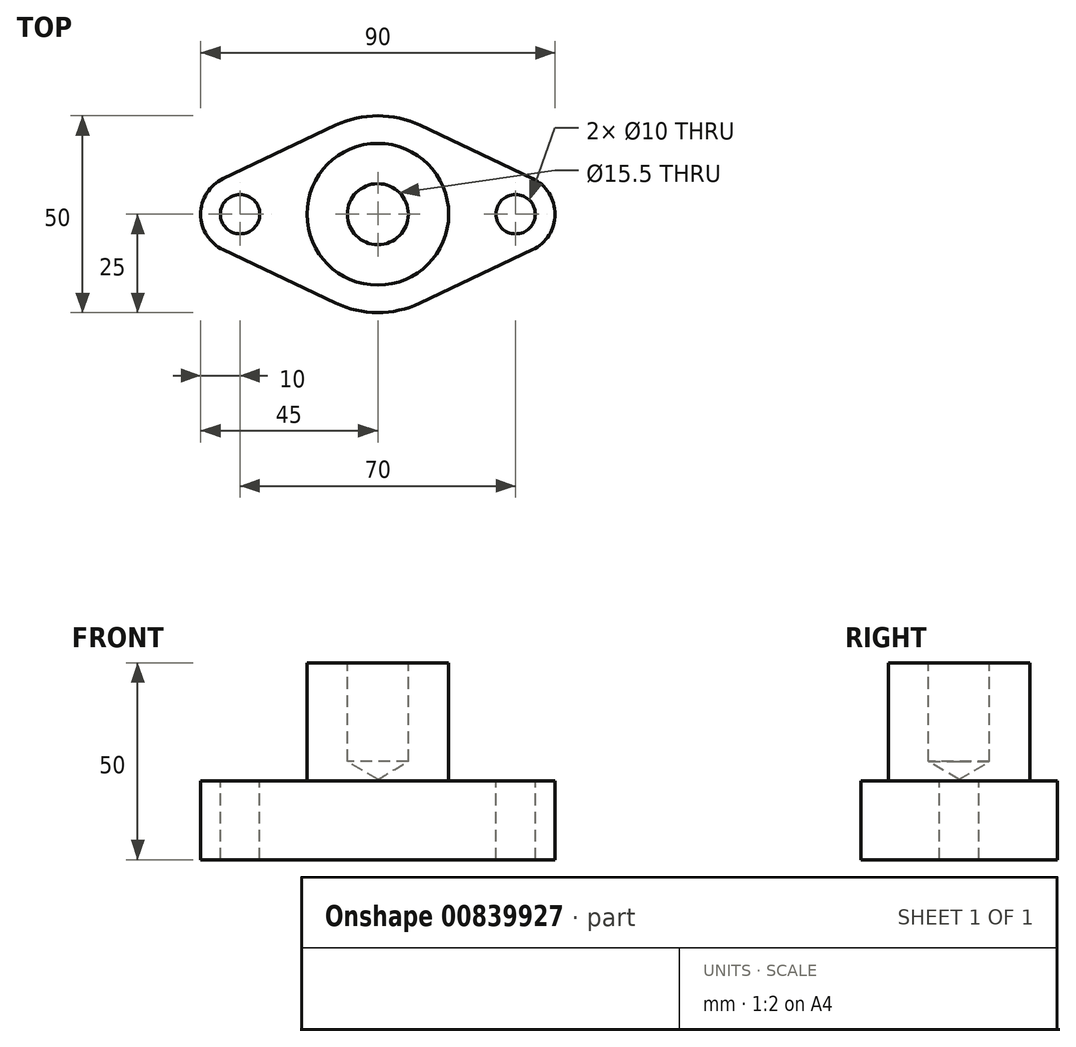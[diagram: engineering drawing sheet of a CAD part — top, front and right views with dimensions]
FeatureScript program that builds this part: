
annotation { "Feature Type Name" : "Feature", "Feature Type Description" : "" }
export const myFeature = defineFeature(function(context is Context, id is Id, definition is map)
    precondition{}
    {
        {
            var Q0;
            Q0=qCreatedBy(makeId("Top.planeOp"),FACE);
            var sketch = newSketch(context, id + "F0", { "sketchPlane" : qUnion([Q0])});
            skLineSegment(sketch, "E0", {"start": v(-39.29, 9.04) * mm, "end": v(-10.71, 22.59) * mm});
            skLineSegment(sketch, "E1", {"start": v(10.71, 22.59) * mm, "end": v(39.29, 9.04) * mm});
            skLineSegment(sketch, "E2", {"start": v(-39.29, -9.04) * mm, "end": v(-10.71, -22.59) * mm});
            skLineSegment(sketch, "E3", {"start": v(10.65, -22.62) * mm, "end": v(39.29, -9.04) * mm});
            skArc(sketch, "E4", {"start": v(-10.71, 22.59) * mm, "mid": v(0, 25) * mm, "end": v(10.71, 22.59) * mm});
            skArc(sketch, "E5", {"start": v(10.65, -22.62) * mm, "mid": v(-0.07, -25) * mm, "end": v(-10.77, -22.56) * mm});
            skArc(sketch, "E6", {"start": v(-39.29, 9.04) * mm, "mid": v(-45, 0) * mm, "end": v(-39.29, -9.04) * mm});
            skArc(sketch, "E7", {"start": v(39.29, 9.04) * mm, "mid": v(45, 0) * mm, "end": v(39.29, -9.04) * mm});
            skSolve(sketch);
        }
        {
            var Q0;
            Q0=makeQuery(id+"F0.imprint","IMPRINT",FACE,{"disambiguationData":[TD([[makeQuery(id+"F0.imprint","IMPRINT",EDGE,{"derivedFrom":sQuery(id+"F0.wireOp",EDGE,"E0")}),-1.0]])]});
            extrude(context, id + "F1", {"entities" : qUnion([Q0]), "depth" : 20 * mm, "offsetDistance" : 25 * mm});
        }
        {
            var Q0;
            Q0=makeQuery(id+"F1.opExtrude","CAP_FACE",FACE,{"disambiguationData":[OSD([sQuery(id+"F0.wireOp",EDGE,"E0"),sQuery(id+"F0.wireOp",EDGE,"E1"),sQuery(id+"F0.wireOp",EDGE,"E2"),sQuery(id+"F0.wireOp",EDGE,"E3"),sQuery(id+"F0.wireOp",EDGE,"E4"),sQuery(id+"F0.wireOp",EDGE,"E5"),sQuery(id+"F0.wireOp",EDGE,"E6"),sQuery(id+"F0.wireOp",EDGE,"E7")])],"isStart":false});
            var sketch = newSketch(context, id + "F2", { "sketchPlane" : qUnion([Q0])});
            skPoint(sketch, "E8", {"position": v(-35, 0) * mm});
            skPoint(sketch, "E9", {"position": v(35, 0) * mm});
            skSolve(sketch);
        }
        {
            var Q0;
            Q0=sQuery(id+"F2.wireOp",VERTEX,"E8");
            var Q1;
            Q1=sQuery(id+"F2.wireOp",VERTEX,"E9");
            var Q2;
            Q2=makeQuery(id+"F1.opExtrude","SWEPT_BODY",BODY,{"disambiguationData":[OSD([sQuery(id+"F0.wireOp",EDGE,"E0"),sQuery(id+"F0.wireOp",EDGE,"E1"),sQuery(id+"F0.wireOp",EDGE,"E2"),sQuery(id+"F0.wireOp",EDGE,"E3"),sQuery(id+"F0.wireOp",EDGE,"E4"),sQuery(id+"F0.wireOp",EDGE,"E5"),sQuery(id+"F0.wireOp",EDGE,"E6"),sQuery(id+"F0.wireOp",EDGE,"E7")])]});
            hole(context, id + "F3", {"style" : HoleStyle.SIMPLE, "endStyle" : HoleEndStyle.BLIND, "holeDiameter" : 10 * mm, "majorDiameter" : 5 * mm, "holeDepth" : 20 * mm, "isTappedThrough" : true, "tappedDepth" : 12 * mm, "tapClearance" : 3, "locations" : qUnion([Q0, Q1]), "scope" : qUnion([Q2])});
        }
        {
            var Q0;
            Q0=makeQuery(id+"F1.opExtrude","CAP_FACE",FACE,{"disambiguationData":[OSD([sQuery(id+"F0.wireOp",EDGE,"E0"),sQuery(id+"F0.wireOp",EDGE,"E1"),sQuery(id+"F0.wireOp",EDGE,"E2"),sQuery(id+"F0.wireOp",EDGE,"E3"),sQuery(id+"F0.wireOp",EDGE,"E4"),sQuery(id+"F0.wireOp",EDGE,"E5"),sQuery(id+"F0.wireOp",EDGE,"E6"),sQuery(id+"F0.wireOp",EDGE,"E7")])],"isStart":false});
            var sketch = newSketch(context, id + "F4", { "sketchPlane" : qUnion([Q0])});
            skCircle(sketch, "E10", {"center": v(0, 0) * mm, "radius": 18 * mm});
            skSolve(sketch);
        }
        {
            var Q0;
            Q0=makeQuery(id+"F4.imprint","IMPRINT",FACE,{"disambiguationData":[TD([[makeQuery(id+"F4.imprint","IMPRINT",EDGE,{"derivedFrom":sQuery(id+"F4.wireOp",EDGE,"E10")}),1.0]])]});
            extrude(context, id + "F5", {"entities" : qUnion([Q0]), "operationType" : NewBodyOperationType.ADD, "depth" : 30 * mm, "offsetDistance" : 25 * mm});
        }
        {
            var Q0;
            Q0=makeQuery(id+"F5.opExtrude","CAP_FACE",FACE,{"disambiguationData":[OSD([sQuery(id+"F4.wireOp",EDGE,"E10")])],"isStart":false});
            var sketch = newSketch(context, id + "F6", { "sketchPlane" : qUnion([Q0])});
            skPoint(sketch, "E11", {"position": v(0, 0) * mm});
            skSolve(sketch);
        }
        {
            var Q0;
            Q0=sQuery(id+"F6.wireOp",VERTEX,"E11");
            var Q1;
            Q1=makeQuery(id+"F1.opExtrude","SWEPT_BODY",BODY,{"disambiguationData":[OSD([sQuery(id+"F0.wireOp",EDGE,"E0"),sQuery(id+"F0.wireOp",EDGE,"E1"),sQuery(id+"F0.wireOp",EDGE,"E2"),sQuery(id+"F0.wireOp",EDGE,"E3"),sQuery(id+"F0.wireOp",EDGE,"E4"),sQuery(id+"F0.wireOp",EDGE,"E5"),sQuery(id+"F0.wireOp",EDGE,"E6"),sQuery(id+"F0.wireOp",EDGE,"E7")])]});
            hole(context, id + "F7", {"style" : HoleStyle.SIMPLE, "endStyle" : HoleEndStyle.BLIND, "standardTappedOrClearance" : lookupTablePath({ "fit" : "Normal", "standard" : "ISO", "size" : "M14", "type" : "Clearance" }), "standardBlindInLast" : lookupTablePath({ "fit" : "Standard", "standard" : "ISO", "size" : "M14", "type" : "Clearance" }), "holeDiameter" : 15.5 * mm, "majorDiameter" : 5 * mm, "holeDepth" : 25 * mm, "isTappedThrough" : true, "tappedDepth" : 12 * mm, "tapClearance" : 3, "locations" : qUnion([Q0]), "scope" : qUnion([Q1])});
        }
    });
